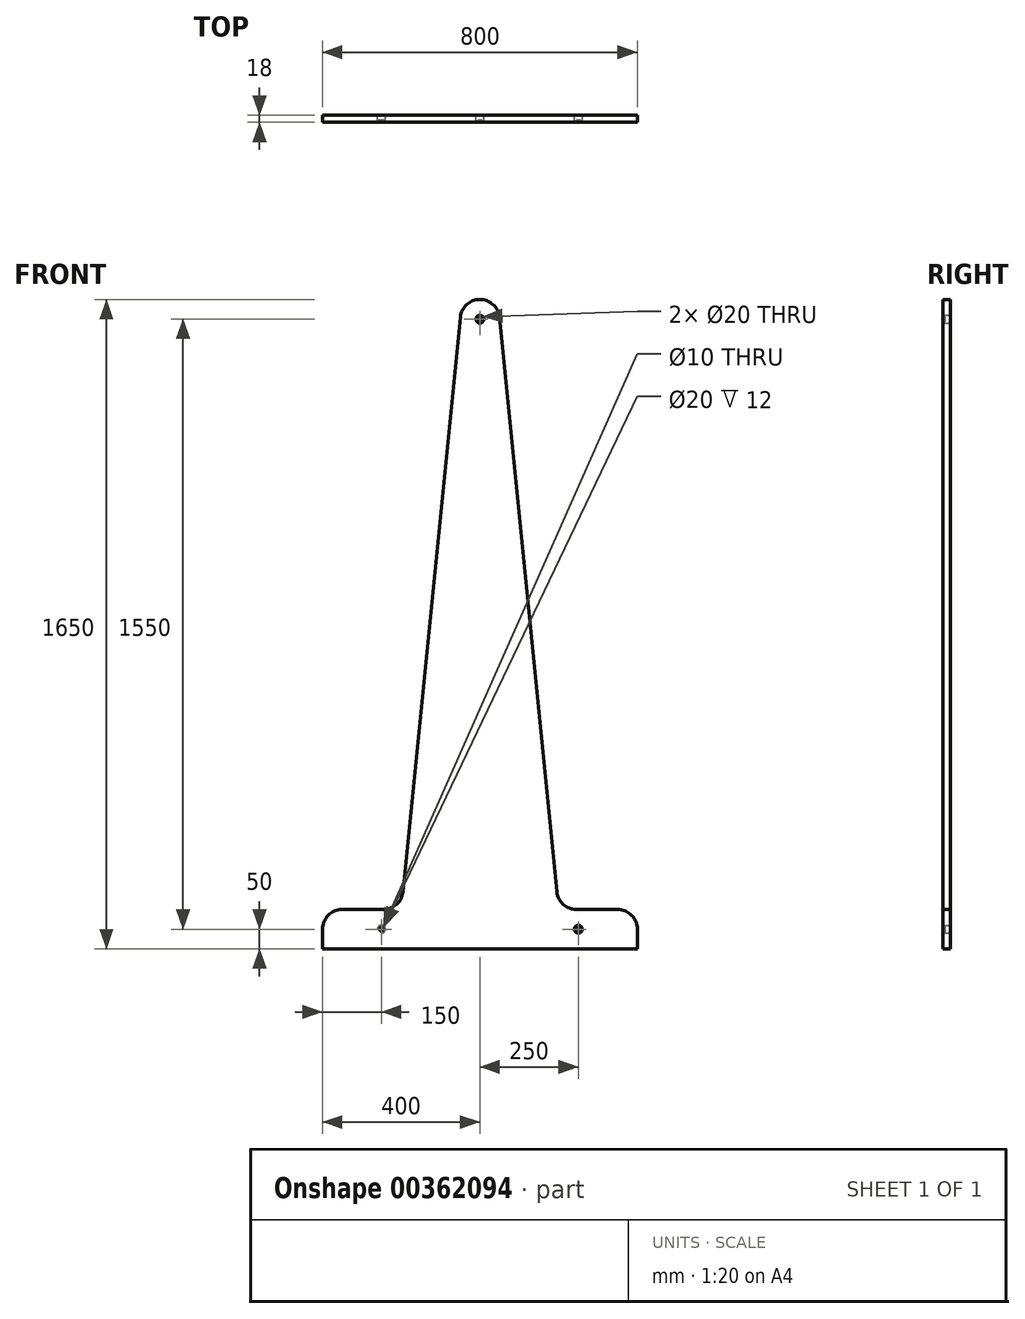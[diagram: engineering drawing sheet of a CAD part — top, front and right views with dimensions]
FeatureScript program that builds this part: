
annotation { "Feature Type Name" : "Feature", "Feature Type Description" : "" }
export const myFeature = defineFeature(function(context is Context, id is Id, definition is map)
    precondition{}
    {
        {
            assignVariable(context, id + "F0", {"name" : "vaneri", "anyValue" : 18});
        }
        {
            var Q0;
            Q0=qCreatedBy(makeId("Front.planeOp"),FACE);
            var sketch = newSketch(context, id + "F1", { "sketchPlane" : qUnion([Q0])});
            skLineSegment(sketch, "E0", {"start": v(0, 0) * mm, "end": v(-400, 0) * mm});
            skLineSegment(sketch, "E1", {"start": v(-400, 0) * mm, "end": v(-400, 50) * mm});
            skLineSegment(sketch, "E2", {"start": v(-350, 100) * mm, "end": v(-245.26, 100) * mm});
            skLineSegment(sketch, "E3", {"start": v(-195.5, 145.03) * mm, "end": v(-49.75, 1604.97) * mm});
            skPoint(sketch, "E4.visualSharp", {"position": v(-200, 100) * mm});
            skArc(sketch, "E4.filletArc", {"start": v(-245.26, 100) * mm, "mid": v(-211.7, 112.93) * mm, "end": v(-195.5, 145.03) * mm});
            skPoint(sketch, "E5.visualSharp", {"position": v(-400, 100) * mm});
            skArc(sketch, "E5.filletArc", {"start": v(-350, 100) * mm, "mid": v(-385.36, 85.36) * mm, "end": v(-400, 50) * mm});
            skCircle(sketch, "E6", {"center": v(-250, 50) * mm, "radius": 10 * mm});
            skCircle(sketch, "E7", {"center": v(-250, 50) * mm, "radius": 5 * mm});
            skCircle(sketch, "E8.MirrorC", {"center": v(250, 50) * mm, "radius": 5 * mm});
            skLineSegment(sketch, "E9.MirrorCS", {"start": v(400, 0) * mm, "end": v(400, 50) * mm});
            skCircle(sketch, "E10.MirrorC", {"center": v(250, 50) * mm, "radius": 10 * mm});
            skArc(sketch, "E11.MirrorCS", {"start": v(350, 100) * mm, "mid": v(385.36, 85.36) * mm, "end": v(400, 50) * mm});
            skArc(sketch, "E12.MirrorCS", {"start": v(245.26, 100) * mm, "mid": v(211.7, 112.93) * mm, "end": v(195.5, 145.03) * mm});
            skLineSegment(sketch, "E13.MirrorCS", {"start": v(0, 0) * mm, "end": v(400, 0) * mm});
            skPoint(sketch, "E14.MirrorP", {"position": v(400, 100) * mm});
            skLineSegment(sketch, "E15.MirrorCS", {"start": v(195.5, 145.03) * mm, "end": v(49.75, 1604.97) * mm});
            skLineSegment(sketch, "E16.MirrorCS", {"start": v(350, 100) * mm, "end": v(245.26, 100) * mm});
            skPoint(sketch, "E17.MirrorP", {"position": v(200, 100) * mm});
            skCircle(sketch, "E18.MirrorC", {"center": v(0, 1600) * mm, "radius": 5 * mm});
            skCircle(sketch, "E19.MirrorC", {"center": v(0, 1600) * mm, "radius": 10 * mm});
            skArc(sketch, "E20", {"start": v(49.75, 1604.97) * mm, "mid": v(0, 1650) * mm, "end": v(-49.75, 1604.97) * mm});
            skSolve(sketch);
        }
        {
            var Q0;
            Q0 = qSketchRegion(id + "F1", true);
            var Q1;
            Q1=makeQuery(id+"F1.imprint","IMPRINT",FACE,{"disambiguationData":[TD([[makeQuery(id+"F1.imprint","IMPRINT",EDGE,{"derivedFrom":sQuery(id+"F1.wireOp",EDGE,"E18.MirrorC")}),1.0]])]});
            var Q2;
            Q2=makeQuery(id+"F1.imprint","IMPRINT",FACE,{"disambiguationData":[TD([[makeQuery(id+"F1.imprint","IMPRINT",EDGE,{"derivedFrom":sQuery(id+"F1.wireOp",EDGE,"E6")}),1.0]])]});
            var Q3;
            Q3=makeQuery(id+"F1.imprint","IMPRINT",FACE,{"disambiguationData":[TD([[makeQuery(id+"F1.imprint","IMPRINT",EDGE,{"derivedFrom":sQuery(id+"F1.wireOp",EDGE,"E8.MirrorC")}),1.0]])]});
            extrude(context, id + "F2", {"entities" : qUnion([Q0, Q1, Q2, Q3]), "depth" : (getVariable(context, 'vaneri')) * mm});
        }
        {
            var Q0;
            Q0=makeQuery(id+"F1.imprint","IMPRINT",FACE,{"disambiguationData":[TD([[makeQuery(id+"F1.imprint","IMPRINT",EDGE,{"derivedFrom":sQuery(id+"F1.wireOp",EDGE,"E18.MirrorC")}),1.0]])]});
            var Q1;
            Q1=makeQuery(id+"F1.imprint","IMPRINT",FACE,{"disambiguationData":[TD([[makeQuery(id+"F1.imprint","IMPRINT",EDGE,{"derivedFrom":sQuery(id+"F1.wireOp",EDGE,"E8.MirrorC")}),1.0]])]});
            var Q2;
            Q2=makeQuery(id+"F1.imprint","IMPRINT",FACE,{"disambiguationData":[TD([[makeQuery(id+"F1.imprint","IMPRINT",EDGE,{"derivedFrom":sQuery(id+"F1.wireOp",EDGE,"E6")}),1.0]])]});
            extrude(context, id + "F3", {"entities" : qUnion([Q0, Q1, Q2]), "operationType" : NewBodyOperationType.REMOVE, "depth" : (getVariable(context, 'vaneri') - 6) * mm});
        }
    });
